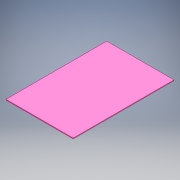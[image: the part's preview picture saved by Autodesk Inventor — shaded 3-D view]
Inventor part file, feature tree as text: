
AUTODESK INVENTOR PART (.ipt)
format: ipt  version: 2018 (Build 220112000, 112)  size: 88,576 bytes
history: native  units: mm
features: extrude x1, sketch x1
ambient origin geometry x8: Origin, YZ Plane, XZ Plane, XY Plane, X Axis, Y Axis, Z Axis, Center Point
bodies: Solid1 (feature_tree)
feature tree (2):
  extrude  "Extrusion1"  Depth=2100.0mm
  sketch  "Sketch1"  dims[d0=1400.0mm d1=2100.0mm d2=16.0mm d3=0.0mm]
